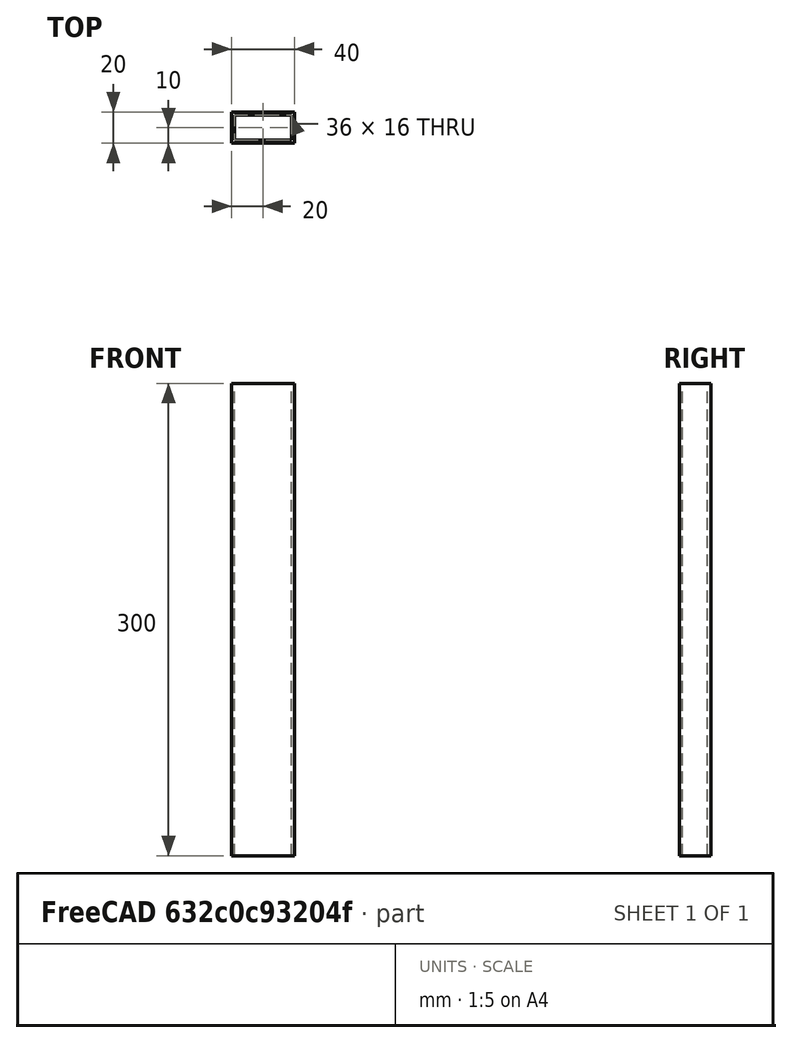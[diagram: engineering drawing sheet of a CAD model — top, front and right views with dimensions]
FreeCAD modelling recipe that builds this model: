
FCSTD DOCUMENT  (FreeCAD 0.20R29177 (Git))
Label: CAM
License: All rights reserved
LicenseURL: http://en.wikipedia.org/wiki/All_rights_reserved
objects: Sketcher::SketchObject×2, PartDesign::Pad×1, PartDesign::Body×1
note: 5 computed .brp shape members not serialized (recipe doc carries the construction recipe); baked Part::Feature solids carry a one-line shape summary decoded from their .brp

FEATURE [Sketcher::SketchObject] Sketch
  FullyConstrained = true
  MapMode = 5
  Support = -> [XY_Plane]
  sketch-geometry (8):
    g0: LineSegment StartX=-20 StartY=-10 StartZ=0 EndX=20 EndY=-10 EndZ=0
    g1: LineSegment StartX=20 StartY=-10 StartZ=0 EndX=20 EndY=10 EndZ=0
    g2: LineSegment StartX=20 StartY=10 StartZ=0 EndX=-20 EndY=10 EndZ=0
    g3: LineSegment StartX=-20 StartY=10 StartZ=0 EndX=-20 EndY=-10 EndZ=0
    g4: LineSegment StartX=-18 StartY=8 StartZ=0 EndX=18 EndY=8 EndZ=0
    g5: LineSegment StartX=18 StartY=8 StartZ=0 EndX=18 EndY=-8 EndZ=0
    g6: LineSegment StartX=18 StartY=-8 StartZ=0 EndX=-18 EndY=-8 EndZ=0
    g7: LineSegment StartX=-18 StartY=-8 StartZ=0 EndX=-18 EndY=8 EndZ=0
  constraints (24):
    c: Coincident(g0,g1)
    c: Coincident(g1,g2)
    c: Coincident(g2,g3)
    c: Coincident(g3,g0)
    c: Horizontal(g0)
    c: Horizontal(g2)
    c: Vertical(g1)
    c: Vertical(g3)
    c: DistanceX(g2,g2) = 40
    c: Distance(g3) = 20
    c: Distance(g-1,g2) = 10
    c: Distance(g-1,g1) = 20
    c: Coincident(g4,g5)
    c: Coincident(g5,g6)
    c: Coincident(g6,g7)
    c: Coincident(g7,g4)
    c: Horizontal(g4)
    c: Horizontal(g6)
    c: Vertical(g5)
    c: Vertical(g7)
    c: Distance(g4,g2) = 2
    c: Distance(g6,g3) = 2
    c: Distance(g5,g1) = 2
    c: Distance(g5,g0) = 2
FEATURE [PartDesign::Pad] Pad
  Direction = (0,0,1)
  Length = 300
  Length2 = 10
  Midplane = true
  Profile = -> Sketch
  ReferenceAxis = -> Sketch [N_Axis]
  Refine = true
  Type = 0
FEATURE [Sketcher::SketchObject] Sketch001
  ExternalGeometry = -> [Pad]
  FullyConstrained = true
  MapMode = 5
  Placement = pos=(0,-10,0) rot=(1,0,0;1.5708rad)
  Support = -> [Pad]
FEATURE [PartDesign::Body] Body  label="tube"
  Group = -> [Sketch,Pad,Sketch001]
  Origin = -> Origin
  Tip = -> Pad
